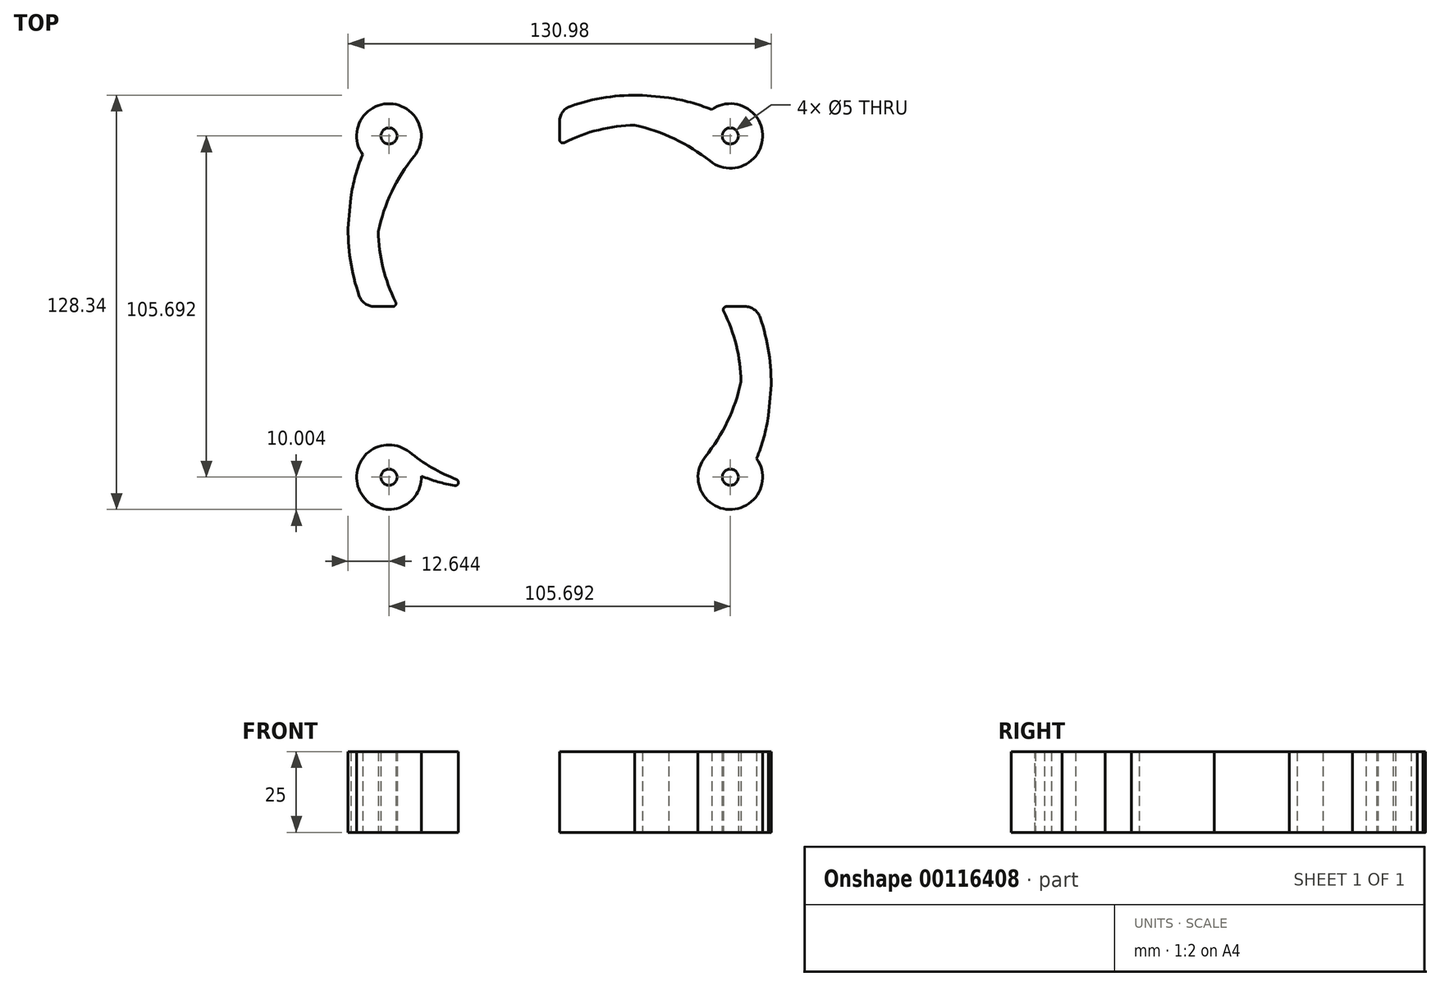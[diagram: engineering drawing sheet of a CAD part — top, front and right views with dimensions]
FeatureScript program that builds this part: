
annotation { "Feature Type Name" : "Feature", "Feature Type Description" : "" }
export const myFeature = defineFeature(function(context is Context, id is Id, definition is map)
    precondition{}
    {
        {
            var Q0;
            Q0=qCreatedBy(makeId("Top.planeOp"),FACE);
            var sketch = newSketch(context, id + "F0", { "sketchPlane" : qUnion([Q0])});
            skCircle(sketch, "E0.cCircle", {"center": v(0, 0) * mm, "radius": 50 * mm, "construction": true});
            skLineSegment(sketch, "E0.0", {"start": v(50, 0) * mm, "end": v(46.2, -19.13) * mm});
            skLineSegment(sketch, "E0.1", {"start": v(46.2, -19.13) * mm, "end": v(35.36, -35.36) * mm});
            skLineSegment(sketch, "E0.2", {"start": v(35.36, -35.36) * mm, "end": v(19.13, -46.2) * mm});
            skLineSegment(sketch, "E0.3", {"start": v(19.13, -46.2) * mm, "end": v(0, -50) * mm});
            skLineSegment(sketch, "E0.4", {"start": v(0, -50) * mm, "end": v(-19.13, -46.2) * mm});
            skLineSegment(sketch, "E0.5", {"start": v(-19.13, -46.2) * mm, "end": v(-35.36, -35.36) * mm});
            skLineSegment(sketch, "E0.6", {"start": v(-35.36, -35.36) * mm, "end": v(-46.2, -19.13) * mm});
            skLineSegment(sketch, "E0.7", {"start": v(-46.2, -19.13) * mm, "end": v(-50, 0) * mm});
            skLineSegment(sketch, "E0.8", {"start": v(-50, 0) * mm, "end": v(-46.2, 19.13) * mm});
            skLineSegment(sketch, "E0.9", {"start": v(-46.2, 19.13) * mm, "end": v(-35.36, 35.36) * mm});
            skLineSegment(sketch, "E0.10", {"start": v(-35.36, 35.36) * mm, "end": v(-19.13, 46.2) * mm});
            skLineSegment(sketch, "E0.11", {"start": v(-19.13, 46.2) * mm, "end": v(0, 50) * mm});
            skLineSegment(sketch, "E0.12", {"start": v(0, 50) * mm, "end": v(19.13, 46.2) * mm});
            skLineSegment(sketch, "E0.13", {"start": v(19.13, 46.2) * mm, "end": v(35.36, 35.36) * mm});
            skLineSegment(sketch, "E0.14", {"start": v(35.36, 35.36) * mm, "end": v(46.2, 19.13) * mm});
            skLineSegment(sketch, "E0.15", {"start": v(46.2, 19.13) * mm, "end": v(50, 0) * mm});
            skLineSegment(sketch, "E1", {"start": v(0, 60.8) * mm, "end": v(0, 50) * mm});
            skLineSegment(sketch, "E2", {"start": v(0, 60.8) * mm, "end": v(-19.13, 46.2) * mm});
            skLineSegment(sketch, "E3.1.0", {"start": v(-23.27, 56.17) * mm, "end": v(-35.36, 35.36) * mm});
            skLineSegment(sketch, "E3.1.1", {"start": v(-23.27, 56.17) * mm, "end": v(-19.13, 46.2) * mm});
            skLineSegment(sketch, "E3.2.0", {"start": v(-42.99, 42.99) * mm, "end": v(-46.2, 19.13) * mm});
            skLineSegment(sketch, "E3.2.1", {"start": v(-42.99, 42.99) * mm, "end": v(-35.36, 35.36) * mm});
            skLineSegment(sketch, "E3.3.0", {"start": v(-56.17, 23.27) * mm, "end": v(-50, 0) * mm});
            skLineSegment(sketch, "E3.3.1", {"start": v(-56.17, 23.27) * mm, "end": v(-46.2, 19.13) * mm});
            skLineSegment(sketch, "E3.4.0", {"start": v(-60.8, 0) * mm, "end": v(-46.2, -19.13) * mm});
            skLineSegment(sketch, "E3.4.1", {"start": v(-60.8, 0) * mm, "end": v(-50, 0) * mm});
            skLineSegment(sketch, "E3.5.0", {"start": v(-56.17, -23.27) * mm, "end": v(-35.36, -35.36) * mm});
            skLineSegment(sketch, "E3.5.1", {"start": v(-56.17, -23.27) * mm, "end": v(-46.2, -19.13) * mm});
            skLineSegment(sketch, "E3.6.0", {"start": v(-42.99, -42.99) * mm, "end": v(-19.13, -46.2) * mm});
            skLineSegment(sketch, "E3.6.1", {"start": v(-42.99, -42.99) * mm, "end": v(-35.36, -35.36) * mm});
            skLineSegment(sketch, "E3.7.0", {"start": v(-23.27, -56.17) * mm, "end": v(0, -50) * mm});
            skLineSegment(sketch, "E3.7.1", {"start": v(-23.27, -56.17) * mm, "end": v(-19.13, -46.2) * mm});
            skLineSegment(sketch, "E3.8.0", {"start": v(0, -60.8) * mm, "end": v(19.13, -46.2) * mm});
            skLineSegment(sketch, "E3.8.1", {"start": v(0, -60.8) * mm, "end": v(0, -50) * mm});
            skLineSegment(sketch, "E3.9.0", {"start": v(23.27, -56.17) * mm, "end": v(35.36, -35.36) * mm});
            skLineSegment(sketch, "E3.9.1", {"start": v(23.27, -56.17) * mm, "end": v(19.13, -46.2) * mm});
            skLineSegment(sketch, "E3.10.0", {"start": v(42.99, -42.99) * mm, "end": v(46.2, -19.13) * mm});
            skLineSegment(sketch, "E3.10.1", {"start": v(42.99, -42.99) * mm, "end": v(35.36, -35.36) * mm});
            skLineSegment(sketch, "E3.11.0", {"start": v(56.17, -23.27) * mm, "end": v(50, 0) * mm});
            skLineSegment(sketch, "E3.11.1", {"start": v(56.17, -23.27) * mm, "end": v(46.2, -19.13) * mm});
            skLineSegment(sketch, "E3.12.0", {"start": v(60.8, 0) * mm, "end": v(46.2, 19.13) * mm});
            skLineSegment(sketch, "E3.12.1", {"start": v(60.8, 0) * mm, "end": v(50, 0) * mm});
            skLineSegment(sketch, "E3.13.0", {"start": v(56.17, 23.27) * mm, "end": v(35.36, 35.36) * mm});
            skLineSegment(sketch, "E3.13.1", {"start": v(56.17, 23.27) * mm, "end": v(46.2, 19.13) * mm});
            skLineSegment(sketch, "E3.14.0", {"start": v(42.99, 42.99) * mm, "end": v(19.13, 46.2) * mm});
            skLineSegment(sketch, "E3.14.1", {"start": v(42.99, 42.99) * mm, "end": v(35.36, 35.36) * mm});
            skLineSegment(sketch, "E3.15.0", {"start": v(23.27, 56.17) * mm, "end": v(0, 50) * mm});
            skLineSegment(sketch, "E3.15.1", {"start": v(23.27, 56.17) * mm, "end": v(19.13, 46.2) * mm});
            skLineSegment(sketch, "E4", {"start": v(56.37, 56.37) * mm, "end": v(49.32, 49.32) * mm});
            skArc(sketch, "E5", {"start": v(56.37, 56.37) * mm, "mid": v(28.71, 65.3) * mm, "end": v(0, 60.8) * mm});
            skArc(sketch, "E6", {"start": v(49.32, 49.32) * mm, "mid": v(24.75, 56.17) * mm, "end": v(0, 50) * mm});
            skCircle(sketch, "E7", {"center": v(52.85, 52.85) * mm, "radius": 10 * mm});
            skLineSegment(sketch, "E8", {"start": v(25.63, 65.46) * mm, "end": v(53.79, 62.8) * mm});
            skArc(sketch, "E9", {"start": v(46.55, 45.08) * mm, "mid": v(35.55, 51.98) * mm, "end": v(23.27, 56.17) * mm});
            skCircle(sketch, "E10", {"center": v(52.85, 52.85) * mm, "radius": 2.5 * mm});
            skArc(sketch, "E11.1.0", {"start": v(-56.37, 56.37) * mm, "mid": v(-65.3, 28.71) * mm, "end": v(-60.8, 0) * mm});
            skArc(sketch, "E11.1.1", {"start": v(-49.32, 49.32) * mm, "mid": v(-56.17, 24.75) * mm, "end": v(-50, 0) * mm});
            skLineSegment(sketch, "E11.1.3", {"start": v(-65.46, 25.63) * mm, "end": v(-62.8, 53.79) * mm});
            skArc(sketch, "E11.1.4", {"start": v(-45.08, 46.55) * mm, "mid": v(-51.98, 35.55) * mm, "end": v(-56.17, 23.27) * mm});
            skCircle(sketch, "E11.1.5", {"center": v(-52.85, 52.85) * mm, "radius": 10 * mm});
            skCircle(sketch, "E11.1.6", {"center": v(-52.85, 52.85) * mm, "radius": 2.5 * mm});
            skLineSegment(sketch, "E11.1.7", {"start": v(-56.37, 56.37) * mm, "end": v(-49.32, 49.32) * mm});
            skArc(sketch, "E11.2.0", {"start": v(-56.37, -56.37) * mm, "mid": v(-28.71, -65.3) * mm, "end": v(0, -60.8) * mm});
            skArc(sketch, "E11.2.1", {"start": v(-49.32, -49.32) * mm, "mid": v(-24.75, -56.17) * mm, "end": v(0, -50) * mm});
            skLineSegment(sketch, "E11.2.3", {"start": v(-25.63, -65.46) * mm, "end": v(-53.79, -62.8) * mm});
            skArc(sketch, "E11.2.4", {"start": v(-46.55, -45.08) * mm, "mid": v(-35.55, -51.98) * mm, "end": v(-23.27, -56.17) * mm});
            skCircle(sketch, "E11.2.5", {"center": v(-52.85, -52.85) * mm, "radius": 10 * mm});
            skCircle(sketch, "E11.2.6", {"center": v(-52.85, -52.85) * mm, "radius": 2.5 * mm});
            skLineSegment(sketch, "E11.2.7", {"start": v(-56.37, -56.37) * mm, "end": v(-49.32, -49.32) * mm});
            skArc(sketch, "E11.3.0", {"start": v(56.37, -56.37) * mm, "mid": v(65.3, -28.71) * mm, "end": v(60.8, 0) * mm});
            skArc(sketch, "E11.3.1", {"start": v(49.32, -49.32) * mm, "mid": v(56.17, -24.75) * mm, "end": v(50, 0) * mm});
            skLineSegment(sketch, "E11.3.3", {"start": v(65.46, -25.63) * mm, "end": v(62.8, -53.79) * mm});
            skArc(sketch, "E11.3.4", {"start": v(45.08, -46.55) * mm, "mid": v(51.98, -35.55) * mm, "end": v(56.17, -23.27) * mm});
            skCircle(sketch, "E11.3.5", {"center": v(52.85, -52.85) * mm, "radius": 10 * mm});
            skCircle(sketch, "E11.3.6", {"center": v(52.85, -52.85) * mm, "radius": 2.5 * mm});
            skLineSegment(sketch, "E11.3.7", {"start": v(56.37, -56.37) * mm, "end": v(49.32, -49.32) * mm});
            skSolve(sketch);
        }
        {
            var Q0;
            {var subQ5=sQuery(id+"F0.wireOp",EDGE,"E11.1.0");var subQ7=sQuery(id+"F0.wireOp",EDGE,"E11.1.7");var subQ9=makeQuery(id+"F0.imprint","INTERSECT",VERTEX,{"derivedFrom":[subQ5,subQ7]});Q0=makeQuery(id+"F0.imprint","IMPRINT",FACE,{"disambiguationData":[TD([[makeQuery(id+"F0.imprint","IMPRINT",EDGE,{"disambiguationData":[TD([[subQ9,-1.0]])],"derivedFrom":subQ5}),-1.0]])]});}
            var Q1;
            {var subQ0=sQuery(id+"F0.wireOp",EDGE,"E11.1.7");var subQ4=sQuery(id+"F0.wireOp",EDGE,"E11.1.0");var subQ5=makeQuery(id+"F0.imprint","INTERSECT",VERTEX,{"derivedFrom":[subQ4,subQ0]});Q1=makeQuery(id+"F0.imprint","IMPRINT",FACE,{"disambiguationData":[TD([[makeQuery(id+"F0.imprint","IMPRINT",EDGE,{"disambiguationData":[TD([[subQ5,-1.0]])],"derivedFrom":subQ4}),1.0]])]});}
            var Q2;
            {var subQ0=sQuery(id+"F0.wireOp",EDGE,"E3.4.1");Q2=makeQuery(id+"F0.imprint","IMPRINT",FACE,{"disambiguationData":[TD([[makeQuery(id+"F0.imprint","IMPRINT",EDGE,{"derivedFrom":subQ0}),1.0]])]});}
            var Q3;
            {var subQ0=sQuery(id+"F0.wireOp",EDGE,"E11.1.3");var subQ1=sQuery(id+"F0.wireOp",EDGE,"E11.1.0");var subQ2=makeQuery(id+"F0.imprint","INTERSECT",VERTEX,{"disambiguationData":[OD(1.0)],"derivedFrom":[subQ1,subQ0]});Q3=makeQuery(id+"F0.imprint","IMPRINT",FACE,{"disambiguationData":[TD([[makeQuery(id+"F0.imprint","IMPRINT",EDGE,{"disambiguationData":[TD([[subQ2,1.0]])],"derivedFrom":subQ1}),-1.0]])]});}
            var Q4;
            {var subQ0=sQuery(id+"F0.wireOp",EDGE,"E11.1.4");Q4=makeQuery(id+"F0.imprint","IMPRINT",FACE,{"disambiguationData":[TD([[makeQuery(id+"F0.imprint","IMPRINT",EDGE,{"derivedFrom":subQ0}),-1.0]])]});}
            var Q5;
            {var subQ1=sQuery(id+"F0.wireOp",EDGE,"E1");Q5=makeQuery(id+"F0.imprint","IMPRINT",FACE,{"disambiguationData":[TD([[makeQuery(id+"F0.imprint","IMPRINT",EDGE,{"derivedFrom":subQ1}),1.0]])]});}
            var Q6;
            {var subQ0=sQuery(id+"F0.wireOp",EDGE,"E8");var subQ1=sQuery(id+"F0.wireOp",EDGE,"E5");var subQ2=makeQuery(id+"F0.imprint","INTERSECT",VERTEX,{"disambiguationData":[OD(1.0)],"derivedFrom":[subQ1,subQ0]});Q6=makeQuery(id+"F0.imprint","IMPRINT",FACE,{"disambiguationData":[TD([[makeQuery(id+"F0.imprint","IMPRINT",EDGE,{"disambiguationData":[TD([[subQ2,1.0]])],"derivedFrom":subQ1}),-1.0]])]});}
            var Q7;
            {var subQ0=sQuery(id+"F0.wireOp",EDGE,"E9");Q7=makeQuery(id+"F0.imprint","IMPRINT",FACE,{"disambiguationData":[TD([[makeQuery(id+"F0.imprint","IMPRINT",EDGE,{"derivedFrom":subQ0}),-1.0]])]});}
            var Q8;
            {var subQ1=sQuery(id+"F0.wireOp",EDGE,"E4");var subQ5=sQuery(id+"F0.wireOp",EDGE,"E5");var subQ6=makeQuery(id+"F0.imprint","INTERSECT",VERTEX,{"derivedFrom":[subQ1,subQ5]});Q8=makeQuery(id+"F0.imprint","IMPRINT",FACE,{"disambiguationData":[TD([[makeQuery(id+"F0.imprint","IMPRINT",EDGE,{"disambiguationData":[TD([[subQ6,-1.0]])],"derivedFrom":subQ1}),-1.0]])]});}
            var Q9;
            {var subQ1=sQuery(id+"F0.wireOp",EDGE,"E4");var subQ5=sQuery(id+"F0.wireOp",EDGE,"E5");var subQ6=makeQuery(id+"F0.imprint","INTERSECT",VERTEX,{"derivedFrom":[subQ1,subQ5]});Q9=makeQuery(id+"F0.imprint","IMPRINT",FACE,{"disambiguationData":[TD([[makeQuery(id+"F0.imprint","IMPRINT",EDGE,{"disambiguationData":[TD([[subQ6,-1.0]])],"derivedFrom":subQ1}),1.0]])]});}
            var Q10;
            {var subQ0=sQuery(id+"F0.wireOp",EDGE,"E3.12.1");Q10=makeQuery(id+"F0.imprint","IMPRINT",FACE,{"disambiguationData":[TD([[makeQuery(id+"F0.imprint","IMPRINT",EDGE,{"derivedFrom":subQ0}),1.0]])]});}
            var Q11;
            {var subQ0=sQuery(id+"F0.wireOp",EDGE,"E11.3.7");var subQ7=sQuery(id+"F0.wireOp",EDGE,"E11.3.0");var subQ10=makeQuery(id+"F0.imprint","INTERSECT",VERTEX,{"derivedFrom":[subQ7,subQ0]});Q11=makeQuery(id+"F0.imprint","IMPRINT",FACE,{"disambiguationData":[TD([[makeQuery(id+"F0.imprint","IMPRINT",EDGE,{"disambiguationData":[TD([[subQ10,-1.0]])],"derivedFrom":subQ7}),1.0]])]});}
            var Q12;
            {var subQ0=sQuery(id+"F0.wireOp",EDGE,"E11.3.4");Q12=makeQuery(id+"F0.imprint","IMPRINT",FACE,{"disambiguationData":[TD([[makeQuery(id+"F0.imprint","IMPRINT",EDGE,{"derivedFrom":subQ0}),-1.0]])]});}
            var Q13;
            {var subQ0=sQuery(id+"F0.wireOp",EDGE,"E11.3.3");var subQ1=sQuery(id+"F0.wireOp",EDGE,"E11.3.0");var subQ2=makeQuery(id+"F0.imprint","INTERSECT",VERTEX,{"disambiguationData":[OD(1.0)],"derivedFrom":[subQ1,subQ0]});Q13=makeQuery(id+"F0.imprint","IMPRINT",FACE,{"disambiguationData":[TD([[makeQuery(id+"F0.imprint","IMPRINT",EDGE,{"disambiguationData":[TD([[subQ2,1.0]])],"derivedFrom":subQ1}),-1.0]])]});}
            var Q14;
            {var subQ4=sQuery(id+"F0.wireOp",EDGE,"E11.3.7");var subQ5=sQuery(id+"F0.wireOp",EDGE,"E11.3.0");var subQ6=makeQuery(id+"F0.imprint","INTERSECT",VERTEX,{"derivedFrom":[subQ5,subQ4]});Q14=makeQuery(id+"F0.imprint","IMPRINT",FACE,{"disambiguationData":[TD([[makeQuery(id+"F0.imprint","IMPRINT",EDGE,{"disambiguationData":[TD([[subQ6,-1.0]])],"derivedFrom":subQ5}),-1.0]])]});}
            var Q15;
            {var subQ5=sQuery(id+"F0.wireOp",EDGE,"E11.2.0");var subQ7=sQuery(id+"F0.wireOp",EDGE,"E11.2.7");var subQ9=makeQuery(id+"F0.imprint","INTERSECT",VERTEX,{"derivedFrom":[subQ5,subQ7]});Q15=makeQuery(id+"F0.imprint","IMPRINT",FACE,{"disambiguationData":[TD([[makeQuery(id+"F0.imprint","IMPRINT",EDGE,{"disambiguationData":[TD([[subQ9,-1.0]])],"derivedFrom":subQ5}),-1.0]])]});}
            var Q16;
            {var subQ1=sQuery(id+"F0.wireOp",EDGE,"E11.2.0");var subQ5=sQuery(id+"F0.wireOp",EDGE,"E11.2.7");var subQ10=makeQuery(id+"F0.imprint","INTERSECT",VERTEX,{"derivedFrom":[subQ1,subQ5]});Q16=makeQuery(id+"F0.imprint","IMPRINT",FACE,{"disambiguationData":[TD([[makeQuery(id+"F0.imprint","IMPRINT",EDGE,{"disambiguationData":[TD([[subQ10,-1.0]])],"derivedFrom":subQ1}),1.0]])]});}
            var Q17;
            {var subQ0=sQuery(id+"F0.wireOp",EDGE,"E11.2.4");Q17=makeQuery(id+"F0.imprint","IMPRINT",FACE,{"disambiguationData":[TD([[makeQuery(id+"F0.imprint","IMPRINT",EDGE,{"derivedFrom":subQ0}),-1.0]])]});}
            var Q18;
            {var subQ0=sQuery(id+"F0.wireOp",EDGE,"E3.8.1");Q18=makeQuery(id+"F0.imprint","IMPRINT",FACE,{"disambiguationData":[TD([[makeQuery(id+"F0.imprint","IMPRINT",EDGE,{"derivedFrom":subQ0}),1.0]])]});}
            var Q19;
            {var subQ0=sQuery(id+"F0.wireOp",EDGE,"E11.2.3");var subQ1=sQuery(id+"F0.wireOp",EDGE,"E11.2.0");var subQ2=makeQuery(id+"F0.imprint","INTERSECT",VERTEX,{"disambiguationData":[OD(1.0)],"derivedFrom":[subQ1,subQ0]});Q19=makeQuery(id+"F0.imprint","IMPRINT",FACE,{"disambiguationData":[TD([[makeQuery(id+"F0.imprint","IMPRINT",EDGE,{"disambiguationData":[TD([[subQ2,1.0]])],"derivedFrom":subQ1}),-1.0]])]});}
            extrude(context, id + "F1", {"entities" : qUnion([Q0, Q1, Q2, Q3, Q4, Q5, Q6, Q7, Q8, Q9, Q10, Q11, Q12, Q13, Q14, Q15, Q16, Q17, Q18, Q19]), "endBound" : BoundingType.SYMMETRIC, "depth" : 25 * mm});
        }
        {
            var Q0;
            Q0=makeQuery(id+"F1.opExtrude","SWEPT_EDGE",EDGE,{"disambiguationData":[OSD([sQuery(id+"F0.wireOp",EDGE,"E0.11"),sQuery(id+"F0.wireOp",EDGE,"E0.12"),sQuery(id+"F0.wireOp",EDGE,"E1"),sQuery(id+"F0.wireOp",EDGE,"E3.15.0"),sQuery(id+"F0.wireOp",EDGE,"E6")])]});
            var Q1;
            Q1=makeQuery(id+"F1.opExtrude","SWEPT_EDGE",EDGE,{"disambiguationData":[OSD([sQuery(id+"F0.wireOp",EDGE,"E0.0"),sQuery(id+"F0.wireOp",EDGE,"E0.15"),sQuery(id+"F0.wireOp",EDGE,"E3.11.0"),sQuery(id+"F0.wireOp",EDGE,"E11.3.1"),sQuery(id+"F0.wireOp",EDGE,"E3.12.1")])]});
            var Q2;
            Q2=makeQuery(id+"F1.opExtrude","SWEPT_EDGE",EDGE,{"disambiguationData":[OSD([sQuery(id+"F0.wireOp",EDGE,"E0.7"),sQuery(id+"F0.wireOp",EDGE,"E0.8"),sQuery(id+"F0.wireOp",EDGE,"E3.3.0"),sQuery(id+"F0.wireOp",EDGE,"E11.1.1"),sQuery(id+"F0.wireOp",EDGE,"E3.4.1")])]});
            var Q3;
            Q3=makeQuery(id+"F1.opExtrude","SWEPT_EDGE",EDGE,{"disambiguationData":[OSD([sQuery(id+"F0.wireOp",EDGE,"E0.3"),sQuery(id+"F0.wireOp",EDGE,"E0.4"),sQuery(id+"F0.wireOp",EDGE,"E3.7.0"),sQuery(id+"F0.wireOp",EDGE,"E11.2.1"),sQuery(id+"F0.wireOp",EDGE,"E3.8.1")])]});
            fillet(context, id + "F2", {"entities" : qUnion([Q0, Q1, Q2, Q3]), "radius" : 1 * mm, "tangentPropagation" : true, "allowEdgeOverflow" : false});
        }
        {
            var Q0;
            Q0=makeQuery(id+"F1.opExtrude","SWEPT_EDGE",EDGE,{"disambiguationData":[OSD([sQuery(id+"F0.wireOp",EDGE,"E3.4.0"),sQuery(id+"F0.wireOp",EDGE,"E11.1.0"),sQuery(id+"F0.wireOp",EDGE,"E3.4.1")])]});
            var Q1;
            Q1=makeQuery(id+"F1.opExtrude","SWEPT_EDGE",EDGE,{"disambiguationData":[OSD([sQuery(id+"F0.wireOp",EDGE,"E3.8.0"),sQuery(id+"F0.wireOp",EDGE,"E11.2.0"),sQuery(id+"F0.wireOp",EDGE,"E3.8.1")])]});
            var Q2;
            Q2=makeQuery(id+"F1.opExtrude","SWEPT_EDGE",EDGE,{"disambiguationData":[OSD([sQuery(id+"F0.wireOp",EDGE,"E3.12.0"),sQuery(id+"F0.wireOp",EDGE,"E11.3.0"),sQuery(id+"F0.wireOp",EDGE,"E3.12.1")])]});
            var Q3;
            Q3=makeQuery(id+"F1.opExtrude","SWEPT_EDGE",EDGE,{"disambiguationData":[OSD([sQuery(id+"F0.wireOp",EDGE,"E1"),sQuery(id+"F0.wireOp",EDGE,"E2"),sQuery(id+"F0.wireOp",EDGE,"E5")])]});
            fillet(context, id + "F3", {"entities" : qUnion([Q0, Q1, Q2, Q3]), "radius" : 5 * mm, "tangentPropagation" : true, "allowEdgeOverflow" : false});
        }
    });
